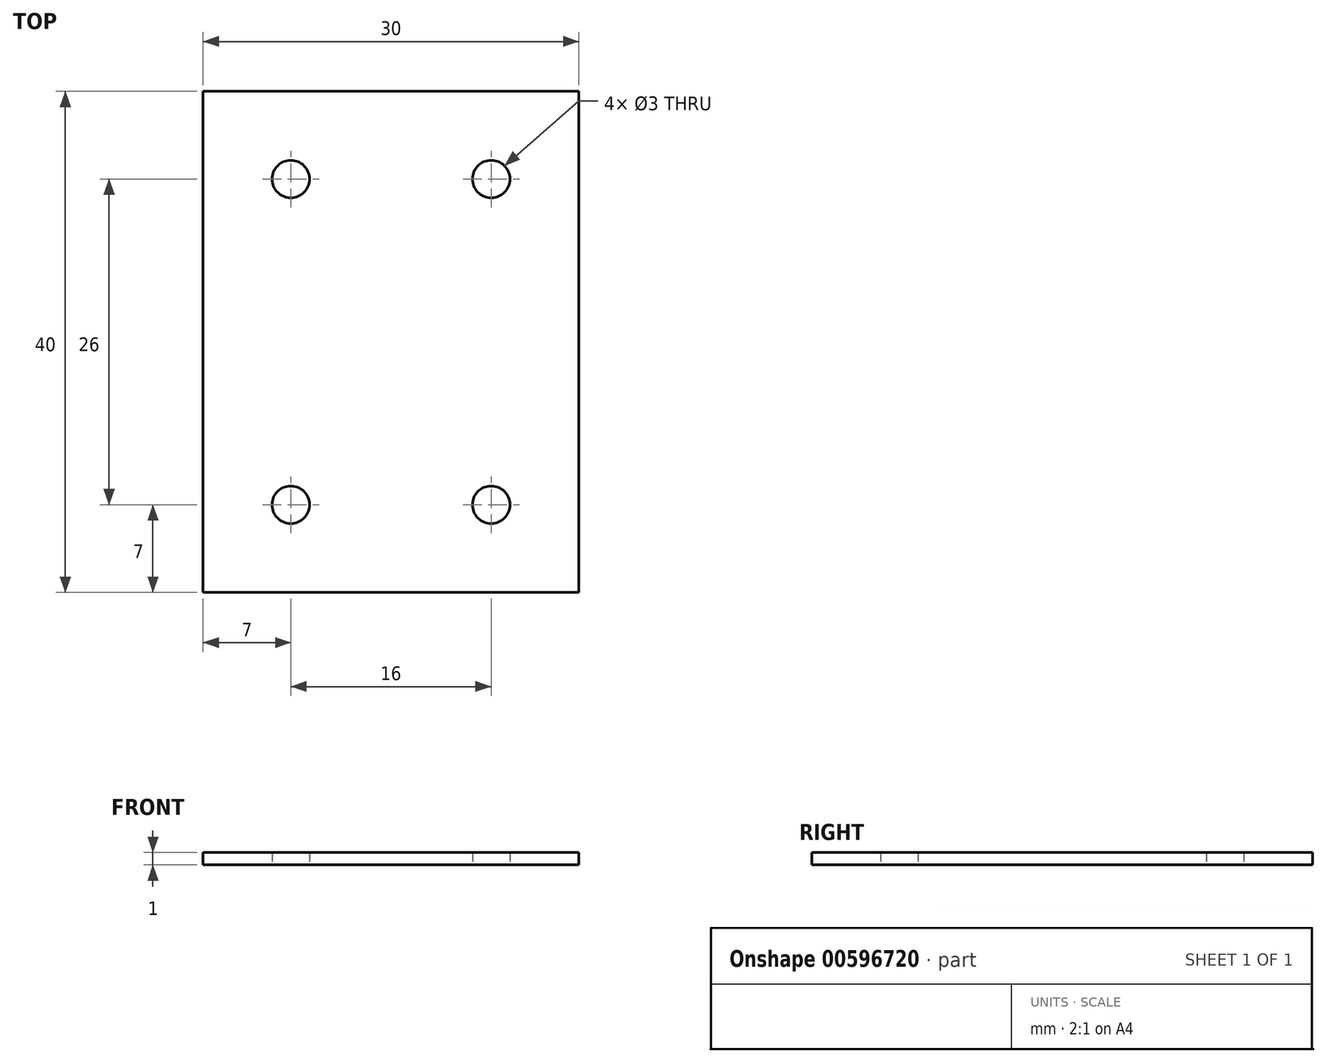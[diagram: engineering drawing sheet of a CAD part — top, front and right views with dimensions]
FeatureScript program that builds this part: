
annotation { "Feature Type Name" : "Feature", "Feature Type Description" : "" }
export const myFeature = defineFeature(function(context is Context, id is Id, definition is map)
    precondition{}
    {
        {
            var Q0;
            Q0=qCreatedBy(makeId("Top.planeOp"),FACE);
            var sketch = newSketch(context, id + "F0", { "sketchPlane" : qUnion([Q0])});
            skLineSegment(sketch, "E0.bottom", {"start": v(0, 0) * mm, "end": v(30, 0) * mm});
            skLineSegment(sketch, "E0.top", {"start": v(0, 40) * mm, "end": v(30, 40) * mm});
            skLineSegment(sketch, "E0.left", {"start": v(0, 0) * mm, "end": v(0, 40) * mm});
            skLineSegment(sketch, "E0.right", {"start": v(30, 0) * mm, "end": v(30, 40) * mm});
            skLineSegment(sketch, "E1", {"start": v(0, 33) * mm, "end": v(7, 33) * mm, "construction": true});
            skCircle(sketch, "E2", {"center": v(7, 33) * mm, "radius": 1.5 * mm});
            skLineSegment(sketch, "E3", {"start": v(15, 0) * mm, "end": v(15, 40) * mm, "construction": true});
            skLineSegment(sketch, "E4", {"start": v(0, 20) * mm, "end": v(30, 20) * mm, "construction": true});
            skCircle(sketch, "E5.MirrorC", {"center": v(7, 7) * mm, "radius": 1.5 * mm});
            skCircle(sketch, "E6.MirrorC", {"center": v(23, 33) * mm, "radius": 1.5 * mm});
            skCircle(sketch, "E7.MirrorC", {"center": v(23, 7) * mm, "radius": 1.5 * mm});
            skSolve(sketch);
        }
        {
            var Q0;
            Q0=makeQuery(id+"F0.imprint","IMPRINT",FACE,{"disambiguationData":[TD([[makeQuery(id+"F0.imprint","IMPRINT",EDGE,{"derivedFrom":sQuery(id+"F0.wireOp",EDGE,"E0.bottom")}),1.0]])]});
            extrude(context, id + "F1", {"entities" : qUnion([Q0]), "depth" : 1 * mm, "offsetDistance" : 25 * mm});
        }
    });
